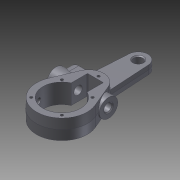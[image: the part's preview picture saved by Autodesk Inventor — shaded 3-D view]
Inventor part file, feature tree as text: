
AUTODESK INVENTOR PART (.ipt)
format: ipt  version: 2011 SP2 (Build 150309200, 309)  size: 242,176 bytes
history: native  units: mm
features: sketch x7, hole x6, extrude x5, plane x2, fillet x2, other x2, chamfer x2
ambient origin geometry x8: Origin, YZ Plane, XZ Plane, XY Plane, X Axis, Y Axis, Z Axis, Center Point
bodies: Solid1 (feature_tree)
feature tree (26):
  extrude  "Extrusion1"  Depth=25.0mm
  extrude  "Extrusion2"  Depth=32.0mm
  plane  "Work Plane1"
  extrude  "Extrusion3"  Depth=125.0mm
  extrude  "Extrusion4"  Depth=14.0mm
  fillet  "Fillet1"  Radius=37.0mm
  fillet  "Fillet2"  Radius=15.0mm
  plane  "Work Plane2"
  extrude  "Extrusion5"  Depth=86.0mm TaperAngle=0.0deg
  hole  "Hole1"  [1 undecoded]
  hole  "Hole2"  [1 undecoded]
  hole  "Hole3"  [1 undecoded]
  hole  "Hole4"  [1 undecoded]
  hole  "Hole5"  [1 undecoded]
  sketch  "Sketch7"  dims[d17=55.0mm d18=10.0mm d19=0.0mm d20=1.0mm d21=1.0mm d22=60.5mm d23=33.0mm d24=14.0mm d25=10.0mm d26=0.0mm d27=10.0mm d28=10.0mm d29=13.0mm d30=6.0mm d31=4.0mm d32=2.0mm d33=90.0deg d34=8.0mm d35=0.0mm d36=10.0mm d37=10.0mm d38=13.8mm d39=6.0mm d40=4.0mm d41=2.0mm d42=90.0deg d43=8.0mm d44=20.594885mm d45=10.0mm d46=10.0mm d47=8.917mm d48=10.0mm d49=4.0mm d50=2.0mm d51=90.0deg d52=10.0mm d53=20.594885mm d54=10.0mm d55=10.0mm d56=15.0mm d57=10.0mm d58=4.0mm d59=2.0mm d60=90.0deg d61=10.0mm d62=0.0mm d64=45.0deg d65=35.5mm d66=60.0mm d67=40.0mm d69=360.0deg d71=4.3mm d72=10.0mm d73=4.0mm d74=2.0mm d75=90.0deg d76=10.0mm d77=20.594885mm d78=15.0deg d79=10.0mm d80=10.0mm d81=8.917mm d82=10.0mm d83=4.0mm d84=2.0mm d85=90.0deg d86=10.0mm d87=0.0mm d88=1.5mm d89=2.0mm d90=45.0deg d91=1.5mm d92=2.0mm d93=45.0deg]
  other  "Work Point1"
  hole  "Hole6"  [1 undecoded]
  chamfer  "Chamfer1"  Distance=14.0mm
  chamfer  "Chamfer2"  Distance=10.0mm
  sketch  "Sketch1"  dims[d0=42.0mm d1=25.0mm]
  sketch  "Sketch2"  dims[d2=44.0mm d3=32.0mm d4=-0.349066mm]
  sketch  "Sketch3"  dims[d5=16.0mm d6=125.0mm]
  sketch  "Sketch4"  dims[d7=1.22173mm d8=14.0mm d9=-0.349066mm d10=37.0mm d11=15.0mm]
  sketch  "Sketch5"  dims[d12=39.5mm d13=86.0mm d14=0.0mm]
  sketch  "Sketch6"  dims[d15=31.0mm d16=26.0mm]
  other  "Work Axis1"
note: 6 required parameter values undecoded (feature->parameter linkage not recoverable at this tier; creation-order binding heuristic only, values carry confidence <= 0.55)
